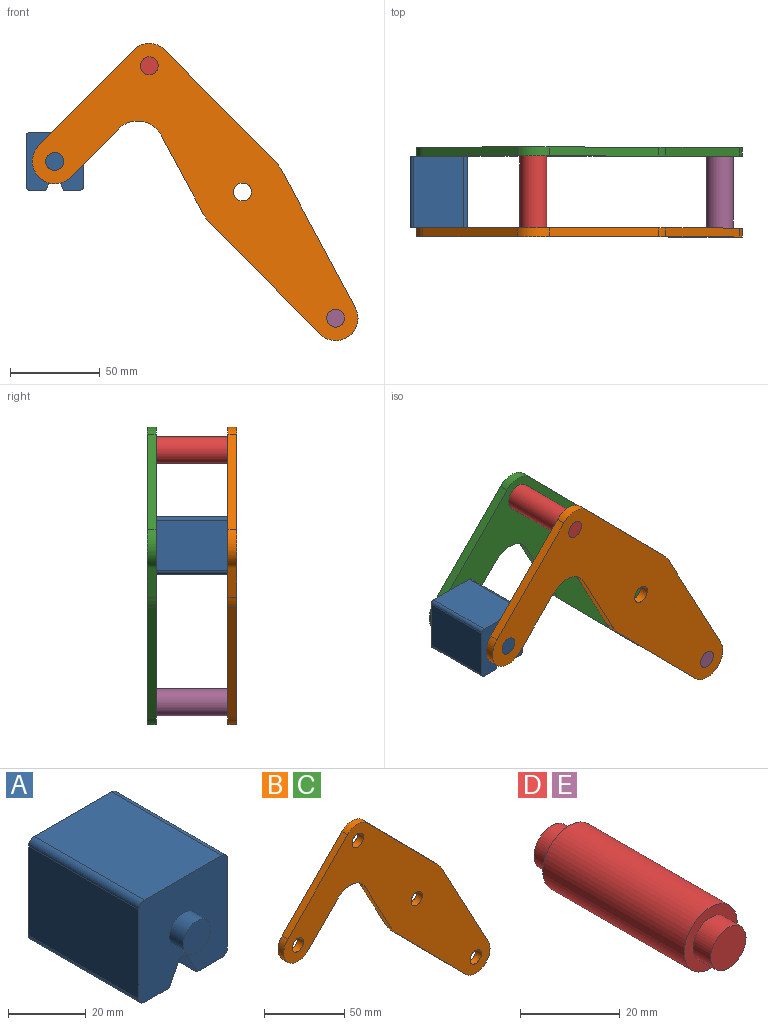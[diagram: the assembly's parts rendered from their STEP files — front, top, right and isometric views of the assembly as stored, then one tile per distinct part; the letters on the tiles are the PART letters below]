
ASSEMBLY  parts=5 mates=3
PART A: 18 faces, bbox 32.1x50x32.1 mm
  f0: plane 40x28.08mm, normal (1,0,0), area 1123.1mm2, adj f4,f10,f13,f14
  f1: plane 40x9.04mm, normal (0,0,-1), area 361.6mm2, adj f2,f4,f10,f14
  f2: plane 40x6.42mm, normal (-0.89,0,-0.45), area 287.2mm2, adj f1,f4,f10,f15
  f3: plane 40x6.42mm, normal (0.89,0,-0.45), area 287.2mm2, adj f4,f5,f10,f15
  f4: plane 32.08x32.08mm, normal (0,-1,0), area 900.6mm2, adj f0,f1,f2,f3,f5,f6,f7,f9
  f5: plane 40x9.04mm, normal (0,0,-1), area 361.6mm2, adj f3,f4,f10,f16
  f6: plane 40x28.08mm, normal (0,0,1), area 1123.1mm2, adj f4,f10,f13,f17
  f7: plane 40x28.08mm, normal (-1,0,0), area 1123.1mm2, adj f4,f10,f16,f17
  f8: plane 10x10mm, normal (0,-1,0), area 78.5mm2, adj f9
  f9: cylinder r=5mm len=10mm, axis (0,1,0), area 157.1mm2, adj f4,f8
  f10: plane 32.08x32.08mm, normal (0,1,0), area 900.6mm2, adj f0,f1,f2,f3,f5,f6,f7,f12
  f11: plane 10x10mm, normal (0,1,0), area 78.5mm2, adj f12
  f12: cylinder r=5mm len=10mm, axis (0,-1,0), area 157.1mm2, adj f10,f11
  f13: cylinder r=2mm len=40mm, axis (0,1,0), area 125.7mm2, adj f0,f4,f6,f10
  f14: cylinder r=2mm len=40mm, axis (0,-1,0), area 125.7mm2, adj f0,f1,f4,f10
  f15: cylinder r=2mm len=40mm, axis (0,1,0), area 177.1mm2, adj f2,f3,f4,f10
  f16: cylinder r=2mm len=40mm, axis (0,1,0), area 125.7mm2, adj f4,f5,f7,f10
  f17: cylinder r=2mm len=40mm, axis (0,-1,0), area 125.7mm2, adj f4,f6,f7,f10
PART B: 18 faces, bbox 181.7x5x165.8 mm
  f0: plane 43.49x23.35mm, normal (-0.88,0,-0.47), area 246.8mm2, adj f1,f14,f16,f17
  f1: cylinder r=25mm len=5.75mm, axis (0,1,0), area 35.8mm2, adj f0,f2,f16,f17
  f2: plane 61.6x60.87mm, normal (-0.71,0,-0.7), area 433mm2, adj f1,f3,f16,f17
  f3: cylinder r=12.5mm len=21.39mm, axis (0,1,0), area 178.4mm2, adj f2,f4,f16,f17
  f4: plane 76.3x40.96mm, normal (0.88,0,0.47), area 433mm2, adj f3,f5,f16,f17
  f5: cylinder r=25mm len=5.75mm, axis (0,1,0), area 35.8mm2, adj f4,f6,f16,f17
  f6: plane 61.6x60.87mm, normal (0.71,0,0.7), area 433mm2, adj f5,f7,f16,f17
  f7: cylinder r=12.5mm len=17.78mm, axis (0,1,0), area 98.9mm2, adj f6,f8,f16,f17
  f8: plane 53.35x52.71mm, normal (-0.71,0,0.7), area 375mm2, adj f7,f9,f16,f17
  f9: cylinder r=12.5mm len=21.39mm, axis (0,1,0), area 196.3mm2, adj f8,f10,f16,f17
  f10: plane 26.86x26.54mm, normal (0.71,0,-0.7), area 188.8mm2, adj f9,f14,f16,f17
  f11: cylinder r=5mm len=10mm, axis (0,1,0), area 157.1mm2, adj f16,f17
  f12: cylinder r=5mm len=10mm, axis (0,1,0), area 157.1mm2, adj f16,f17
  f13: cylinder r=5mm len=10mm, axis (0,1,0), area 157.1mm2, adj f16,f17
  f14: cylinder r=15mm len=23.89mm, axis (0,1,0), area 140.2mm2, adj f0,f10,f16,f17
  f15: cylinder r=5mm len=10mm, axis (0,1,0), area 157.1mm2, adj f16,f17
  f16: plane 181.66x165.78mm, normal (0,-1,0), area 8710.1mm2, adj f0,f1,f2,f3,f4,f5,f6,f7
  f17: plane 181.66x165.78mm, normal (0,1,0), area 8710.1mm2, adj f0,f1,f2,f3,f4,f5,f6,f7
PART C: same geometry as B
PART D: 7 faces, bbox 15x50x15 mm
  f0: cylinder r=7.5mm len=40mm, axis (0,-1,0), area 1885mm2, adj f2,f5
  f1: cylinder r=5mm len=10mm, axis (0,1,0), area 157.1mm2, adj f2,f3
  f2: plane 15x15mm, normal (0,-1,0), area 98.2mm2, adj f0,f1
  f3: plane 10x10mm, normal (0,-1,0), area 78.5mm2, adj f1
  f4: cylinder r=5mm len=10mm, axis (0,-1,0), area 157.1mm2, adj f5,f6
  f5: plane 15x15mm, normal (0,1,0), area 98.2mm2, adj f0,f4
  f6: plane 10x10mm, normal (0,1,0), area 78.5mm2, adj f4
PART E: same geometry as D
PLACE A at identity
PLACE B at identity fixed
PLACE C t=(0,45,0)mm
PLACE D at identity
PLACE E t=(103.95,0,-140.78)mm
MATE fastened C.f7 <-> D.f0  axis (0,-1,0) through (-51.98,40,70.39)mm
MATE revolute A.f9 <-> B.f9  axis (0,1,0) through (-104.69,0,17.04)mm
MATE fastened E.f0 <-> B.f3  axis (0,-1,0) through (51.98,0,-70.39)mm
